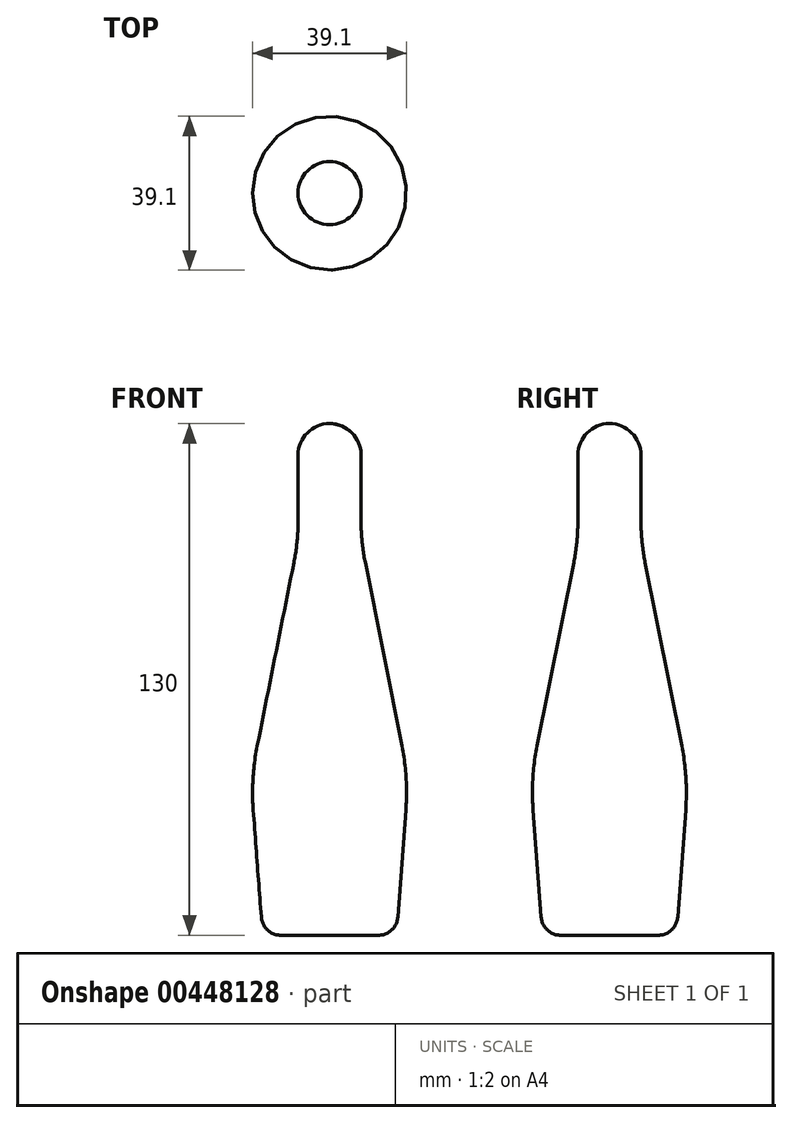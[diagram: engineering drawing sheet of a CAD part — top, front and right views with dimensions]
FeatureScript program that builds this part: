
annotation { "Feature Type Name" : "Feature", "Feature Type Description" : "" }
export const myFeature = defineFeature(function(context is Context, id is Id, definition is map)
    precondition{}
    {
        {
            var Q0;
            Q0=qCreatedBy(makeId("Front.planeOp"),FACE);
            var sketch = newSketch(context, id + "F0", { "sketchPlane" : qUnion([Q0])});
            skLineSegment(sketch, "E0", {"start": v(0, 0) * mm, "end": v(0, 130) * mm});
            skLineSegment(sketch, "E1", {"start": v(0, 0) * mm, "end": v(0, 202.74) * mm, "construction": true});
            skLineSegment(sketch, "E2", {"start": v(0, 0) * mm, "end": v(12.36, 0) * mm});
            skLineSegment(sketch, "E3", {"start": v(17.35, 4.63) * mm, "end": v(19.39, 31.8) * mm});
            skLineSegment(sketch, "E4", {"start": v(18.39, 48.06) * mm, "end": v(9.07, 94.66) * mm});
            skLineSegment(sketch, "E5", {"start": v(8, 105.45) * mm, "end": v(8, 122) * mm});
            skLineSegment(sketch, "E6", {"start": v(0, 130) * mm, "end": v(0, 130) * mm});
            skPoint(sketch, "E7.visualSharp", {"position": v(17, 0) * mm});
            skArc(sketch, "E7.filletArc", {"start": v(12.36, 0) * mm, "mid": v(15.76, 1.33) * mm, "end": v(17.35, 4.63) * mm});
            skPoint(sketch, "E8.visualSharp", {"position": v(20, 40) * mm});
            skArc(sketch, "E8.filletArc", {"start": v(19.39, 31.8) * mm, "mid": v(19.44, 39.97) * mm, "end": v(18.39, 48.06) * mm});
            skPoint(sketch, "E9.visualSharp", {"position": v(8, 100) * mm});
            skArc(sketch, "E9.filletArc", {"start": v(8, 105.45) * mm, "mid": v(8.27, 100.03) * mm, "end": v(9.07, 94.66) * mm});
            skPoint(sketch, "E10.visualSharp", {"position": v(8, 130) * mm});
            skArc(sketch, "E10.filletArc", {"start": v(8, 122) * mm, "mid": v(5.66, 127.66) * mm, "end": v(0, 130) * mm});
            skSolve(sketch);
        }
        {
            var Q0;
            Q0=makeQuery(id+"F0.imprint","IMPRINT",FACE,{"disambiguationData":[TD([[makeQuery(id+"F0.imprint","IMPRINT",EDGE,{"derivedFrom":sQuery(id+"F0.wireOp",EDGE,"E0")}),-1.0]])]});
            var Q1;
            Q1=sQuery(id+"F0.wireOp",EDGE,"E1");
            revolve(context, id + "F1", {"entities" : qUnion([Q0]), "axis" : qUnion([Q1]), "revolveType" : RevolveType.FULL});
        }
    });
